# Revit family: Legrand_Transformateurs_triphasés_de_séparation_des_circuits
name_source: partatom
category: Installations électriques
revit_build: Autodesk Revit 2018 (Build: 20170223_1515(x64)
units: mm (PartAtom-declared; Revit-internal decimal feet)

## family parameters
Basée sur le plan de construction = Non
Conserver l'orientation des annotations = Non
Cote de connecteur circulaire = Utiliser le diamètre
Couper avec des vides une fois chargée = Non
Numéro OmniClass = 23.80.00.00
Partagée = Non
Point de calcul de pièce = Non
Titre OmniClass = Electric Power and Lighting
Toujours verticalement = Oui
Type d'élément = Normal

## types (10) — shared parameters
Caractéristique = Classe I - IP21 - IK08
Conditions Générale d'Utilisation = https://export.legrand.com
Fabricant = Legrand
Modèle = Transformateurs de séparation des circuits
Tension primaire = 400 V en Δ
URL = www.legrand.com

## per-type parameters (varying)
| type | 042540, 042820 | 042541, 042821 | 042542, 042543, 042544, 042822, 042823, 042824 | Isolant | Poids | Section câble primaire | Section câble secondaire | Tension secondaire | Ucc (%) | diamètre de fixation | dimension A | dimension B | dimension C | fixation F | fixation G | perte totale max | perte à vide | puissance |
| Transformateur triphasé 042543 | Non | Non | Oui | classe H | 35.00 kg | 10 mm² | 10 mm² | 230 V en Y +N | 5.2 | 9 mm  [stored 0.0295276 ft] | 420 mm  [stored 1.37795 ft] | 390 mm  [stored 1.27953 ft] | 310 mm  [stored 1.01706 ft] | 400 mm  [stored 1.31234 ft] | 86 mm  [stored 0.282152 ft] | 190 W | 65 W | 3 kVA |
| Transformateur triphasé 042540 | Oui | Non | Non | classe B | 12.00 kg | 4mm² | 4 mm² | 230 V en Y +N | 3.8 | 7 mm  [stored 0.0229659 ft] | 240 mm  [stored 0.787402 ft] | 270 mm  [stored 0.885827 ft] | 190 mm  [stored 0.62336 ft] | 220 mm  [stored 0.721785 ft] | 90 mm  [stored 0.295276 ft] | 52 W | 30 W | 1 kVA |
| Transformateur triphasé 042541 | Non | Oui | Non | classe B | 23.00 kg | 4 mm² | 4 mm² | 230 V en Y +N | 2.7 | 9 mm  [stored 0.0295276 ft] | 370 mm  [stored 1.21391 ft] | 330 mm | 190 mm  [stored 0.62336 ft] | 350 mm  [stored 1.14829 ft] | 69 mm  [stored 0.226378 ft] | 62 W | 38 W | 1 kVA |
| Transformateur triphasé 042542 | Non | Non | Oui | classe H | 27.00 kg | 10 mm² | 10 mm² | 230 V en Y +N | 2.1 | 9 mm  [stored 0.0295276 ft] | 420 mm  [stored 1.37795 ft] | 390 mm  [stored 1.27953 ft] | 310 mm  [stored 1.01706 ft] | 400 mm  [stored 1.31234 ft] | 86 mm  [stored 0.282152 ft] | 147 W | 65 W | 2 kVA |
| Transformateur triphasé 042544 | Non | Non | Oui | classe H | 50.00 kg | 10 mm² | 10 mm² | 230 V en Y +N | 4.1 | 9 mm  [stored 0.0295276 ft] | 420 mm  [stored 1.37795 ft] | 390 mm  [stored 1.27953 ft] | 310 mm  [stored 1.01706 ft] | 400 mm  [stored 1.31234 ft] | 126 mm  [stored 0.413386 ft] | 244 W | 108 W | 4 kVA |
| Transformateur triphasé 042820 | Oui | Non | Non | classe B | 15.00 kg | 4mm² | 4 mm² | 400 V en Y +N | 2.8 | 7 mm  [stored 0.0229659 ft] | 240 mm  [stored 0.787402 ft] | 270 mm  [stored 0.885827 ft] | 190 mm  [stored 0.62336 ft] | 220 mm  [stored 0.721785 ft] | 90 mm  [stored 0.295276 ft] | 74 W | 45 W | 1 kVA |
| Transformateur triphasé 042821 | Non | Oui | Non | classe B | 25.00 kg | 4 mm² | 4 mm² | 400 V en Y +N | 2.0 | 9 mm  [stored 0.0295276 ft] | 370 mm  [stored 1.21391 ft] | 330 mm | 190 mm  [stored 0.62336 ft] | 350 mm  [stored 1.14829 ft] | 69 mm  [stored 0.226378 ft] | 65 W | 35 W | 1 kVA |
| Transformateur triphasé 042822 | Non | Non | Oui | classe H | 31.00 kg | 10 mm² | 10 mm² | 400 V en Y +N | 2.3 | 9 mm  [stored 0.0295276 ft] | 420 mm  [stored 1.37795 ft] | 390 mm  [stored 1.27953 ft] | 310 mm  [stored 1.01706 ft] | 400 mm  [stored 1.31234 ft] | 86 mm  [stored 0.282152 ft] | 120 W | 65 W | 2 kVA |
| Transformateur triphasé 042823 | Non | Non | Oui | classe H | 38.00 kg | 10 mm² | 10 mm² | 400 V en Y +N | 1.9 | 9 mm  [stored 0.0295276 ft] | 420 mm  [stored 1.37795 ft] | 390 mm  [stored 1.27953 ft] | 310 mm  [stored 1.01706 ft] | 400 mm  [stored 1.31234 ft] | 86 mm  [stored 0.282152 ft] | 153 W | 85 W | 3 kVA |
| Transformateur triphasé 042824 | Non | Non | Oui | classe H | 58.00 kg | 10 mm² | 10 mm² | 400 V en Y +N | 2.0 | 9 mm  [stored 0.0295276 ft] | 420 mm  [stored 1.37795 ft] | 390 mm  [stored 1.27953 ft] | 310 mm  [stored 1.01706 ft] | 400 mm  [stored 1.31234 ft] | 126 mm  [stored 0.413386 ft] | 232 W | 108 W | 4 kVA |

note: [stored X ft] marks values corroborated as IEEE doubles in the binary element streams (Revit-internal decimal feet)
